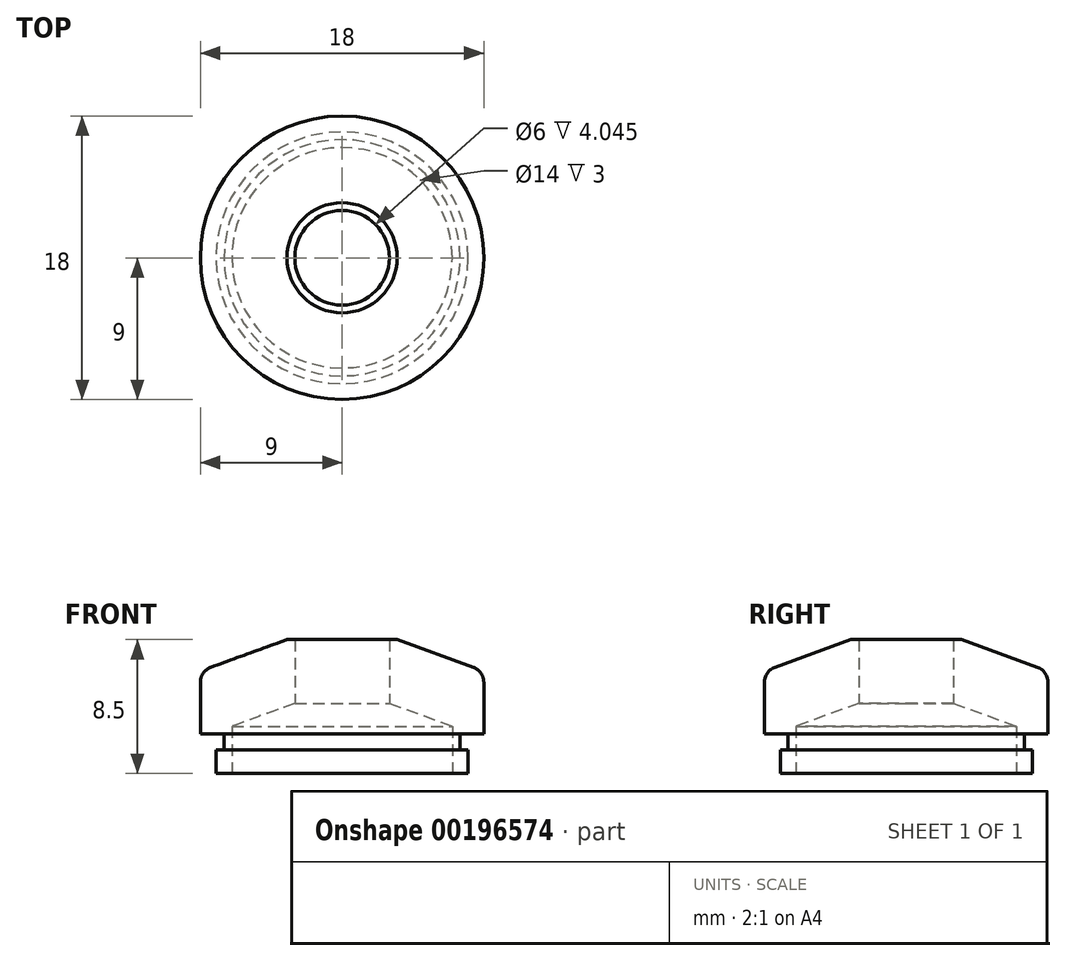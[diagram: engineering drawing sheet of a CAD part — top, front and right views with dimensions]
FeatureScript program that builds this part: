
annotation { "Feature Type Name" : "Feature", "Feature Type Description" : "" }
export const myFeature = defineFeature(function(context is Context, id is Id, definition is map)
    precondition{}
    {
        {
            var Q0;
            Q0=qCreatedBy(makeId("Front.planeOp"),FACE);
            var sketch = newSketch(context, id + "F0", { "sketchPlane" : qUnion([Q0])});
            skLineSegment(sketch, "E0", {"start": v(0, 0) * mm, "end": v(0, 8.5) * mm, "construction": true});
            skLineSegment(sketch, "E1", {"start": v(3, 8.5) * mm, "end": v(3.5, 8.5) * mm});
            skLineSegment(sketch, "E2", {"start": v(3.5, 8.5) * mm, "end": v(8.34, 6.74) * mm});
            skLineSegment(sketch, "E3", {"start": v(9, 5.8) * mm, "end": v(9, 2.5) * mm});
            skLineSegment(sketch, "E4", {"start": v(9, 2.5) * mm, "end": v(7.5, 2.5) * mm});
            skLineSegment(sketch, "E5", {"start": v(7.5, 2.5) * mm, "end": v(7.5, 1.5) * mm});
            skLineSegment(sketch, "E6", {"start": v(7.5, 1.5) * mm, "end": v(8, 1.5) * mm});
            skLineSegment(sketch, "E7", {"start": v(8, 1.5) * mm, "end": v(8, 0) * mm});
            skLineSegment(sketch, "E8", {"start": v(8, 0) * mm, "end": v(7, 0) * mm});
            skLineSegment(sketch, "E9", {"start": v(3, 8.5) * mm, "end": v(3, 4.45) * mm});
            skLineSegment(sketch, "E10", {"start": v(3, 4.45) * mm, "end": v(7, 3) * mm});
            skLineSegment(sketch, "E11", {"start": v(7, 3) * mm, "end": v(7, 0) * mm});
            skPoint(sketch, "E12.visualSharp", {"position": v(9, 6.5) * mm});
            skArc(sketch, "E12.filletArc", {"start": v(9, 5.8) * mm, "mid": v(8.82, 6.37) * mm, "end": v(8.34, 6.74) * mm});
            skSolve(sketch);
        }
        {
            var Q0;
            Q0 = qSketchRegion(id + "F0", true);
            var Q1;
            Q1=sQuery(id+"F0.wireOp",EDGE,"E0");
            revolve(context, id + "F1", {"entities" : qUnion([Q0]), "axis" : qUnion([Q1]), "revolveType" : RevolveType.FULL});
        }
    });
